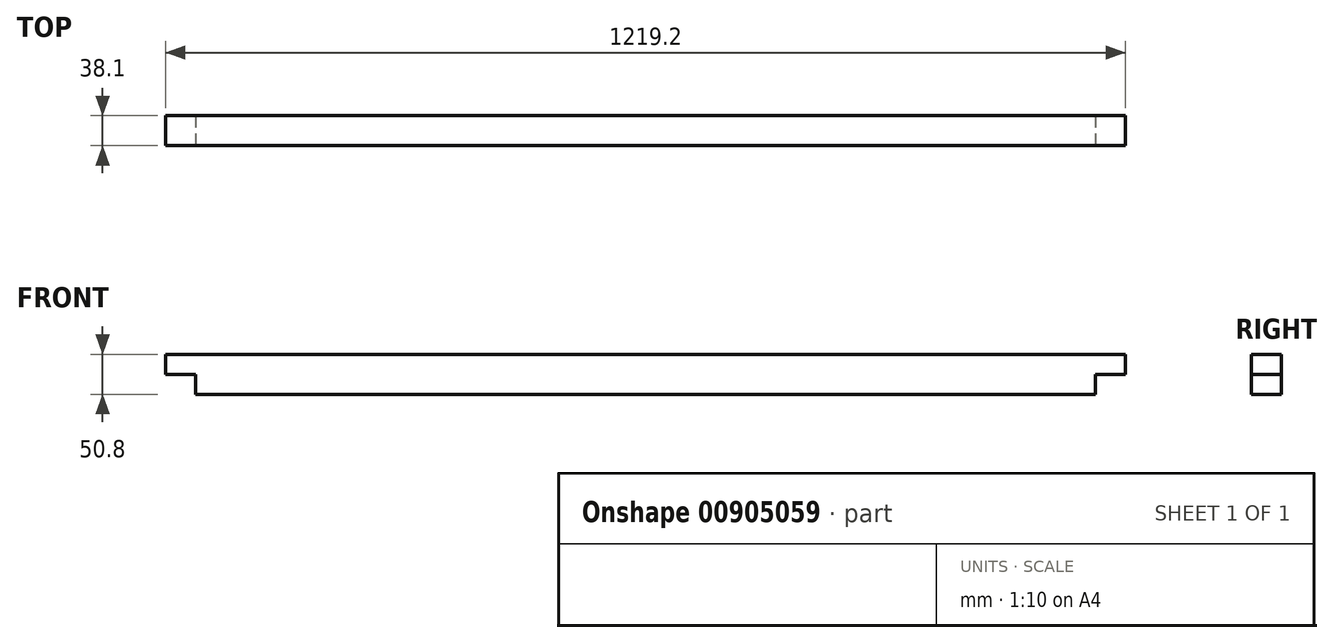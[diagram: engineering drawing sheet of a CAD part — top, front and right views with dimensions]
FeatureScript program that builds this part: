
annotation { "Feature Type Name" : "Feature", "Feature Type Description" : "" }
export const myFeature = defineFeature(function(context is Context, id is Id, definition is map)
    precondition{}
    {
        {
            var Q0;
            Q0=qCreatedBy(makeId("Top.planeOp"),FACE);
            var sketch = newSketch(context, id + "F0", { "sketchPlane" : qUnion([Q0])});
            skLineSegment(sketch, "E0.bottom", {"start": v(609.6, -19.05) * mm, "end": v(-609.6, -19.05) * mm});
            skLineSegment(sketch, "E0.top", {"start": v(609.6, 19.05) * mm, "end": v(-609.6, 19.05) * mm});
            skLineSegment(sketch, "E0.left", {"start": v(609.6, -19.05) * mm, "end": v(609.6, 19.05) * mm});
            skLineSegment(sketch, "E0.right", {"start": v(-609.6, -19.05) * mm, "end": v(-609.6, 19.05) * mm});
            skPoint(sketch, "E0.middle", {"position": v(0, 0) * mm});
            skSolve(sketch);
        }
        {
            var Q0;
            Q0 = qSketchRegion(id + "F0", true);
            extrude(context, id + "F1", {"entities" : qUnion([Q0]), "depth" : 50.8 * mm, "offsetDistance" : 25.4 * mm});
        }
        {
            var Q0;
            Q0=makeQuery(id+"F1.opExtrude","SWEPT_FACE",FACE,{"disambiguationData":[OSD([sQuery(id+"F0.wireOp",EDGE,"E0.bottom")])]});
            var sketch = newSketch(context, id + "F2", { "sketchPlane" : qUnion([Q0])});
            skLineSegment(sketch, "E1", {"start": v(-609.6, 25.4) * mm, "end": v(-571.5, 25.4) * mm, "construction": true});
            skLineSegment(sketch, "E2", {"start": v(-571.5, 25.4) * mm, "end": v(-571.5, 0) * mm, "construction": true});
            skLineSegment(sketch, "E3.bottom", {"start": v(-571.5, 25.4) * mm, "end": v(-609.6, 25.4) * mm});
            skLineSegment(sketch, "E3.top", {"start": v(-571.5, 0) * mm, "end": v(-609.6, 0) * mm});
            skLineSegment(sketch, "E3.left", {"start": v(-571.5, 25.4) * mm, "end": v(-571.5, 0) * mm});
            skLineSegment(sketch, "E3.right", {"start": v(-609.6, 25.4) * mm, "end": v(-609.6, 0) * mm});
            skLineSegment(sketch, "E4", {"start": v(609.6, 25.4) * mm, "end": v(571.5, 25.4) * mm, "construction": true});
            skLineSegment(sketch, "E5", {"start": v(571.5, 25.4) * mm, "end": v(571.5, 0) * mm, "construction": true});
            skLineSegment(sketch, "E6.bottom", {"start": v(571.5, 25.4) * mm, "end": v(609.6, 25.4) * mm});
            skLineSegment(sketch, "E6.top", {"start": v(571.5, 0) * mm, "end": v(609.6, 0) * mm});
            skLineSegment(sketch, "E6.left", {"start": v(571.5, 25.4) * mm, "end": v(571.5, 0) * mm});
            skLineSegment(sketch, "E6.right", {"start": v(609.6, 25.4) * mm, "end": v(609.6, 0) * mm});
            skSolve(sketch);
        }
        {
            var Q0;
            Q0=makeQuery(id+"F2.imprint","IMPRINT",FACE,{"disambiguationData":[TD([[makeQuery(id+"F2.imprint","IMPRINT",EDGE,{"derivedFrom":sQuery(id+"F2.wireOp",EDGE,"E6.bottom")}),-1.0]])]});
            var Q1;
            Q1=makeQuery(id+"F2.imprint","IMPRINT",FACE,{"disambiguationData":[TD([[makeQuery(id+"F2.imprint","IMPRINT",EDGE,{"derivedFrom":sQuery(id+"F2.wireOp",EDGE,"E3.bottom")}),1.0]])]});
            extrude(context, id + "F3", {"entities" : qUnion([Q0, Q1]), "operationType" : NewBodyOperationType.REMOVE, "oppositeDirection" : true, "depth" : 38.1 * mm, "offsetDistance" : 25.4 * mm});
        }
    });
